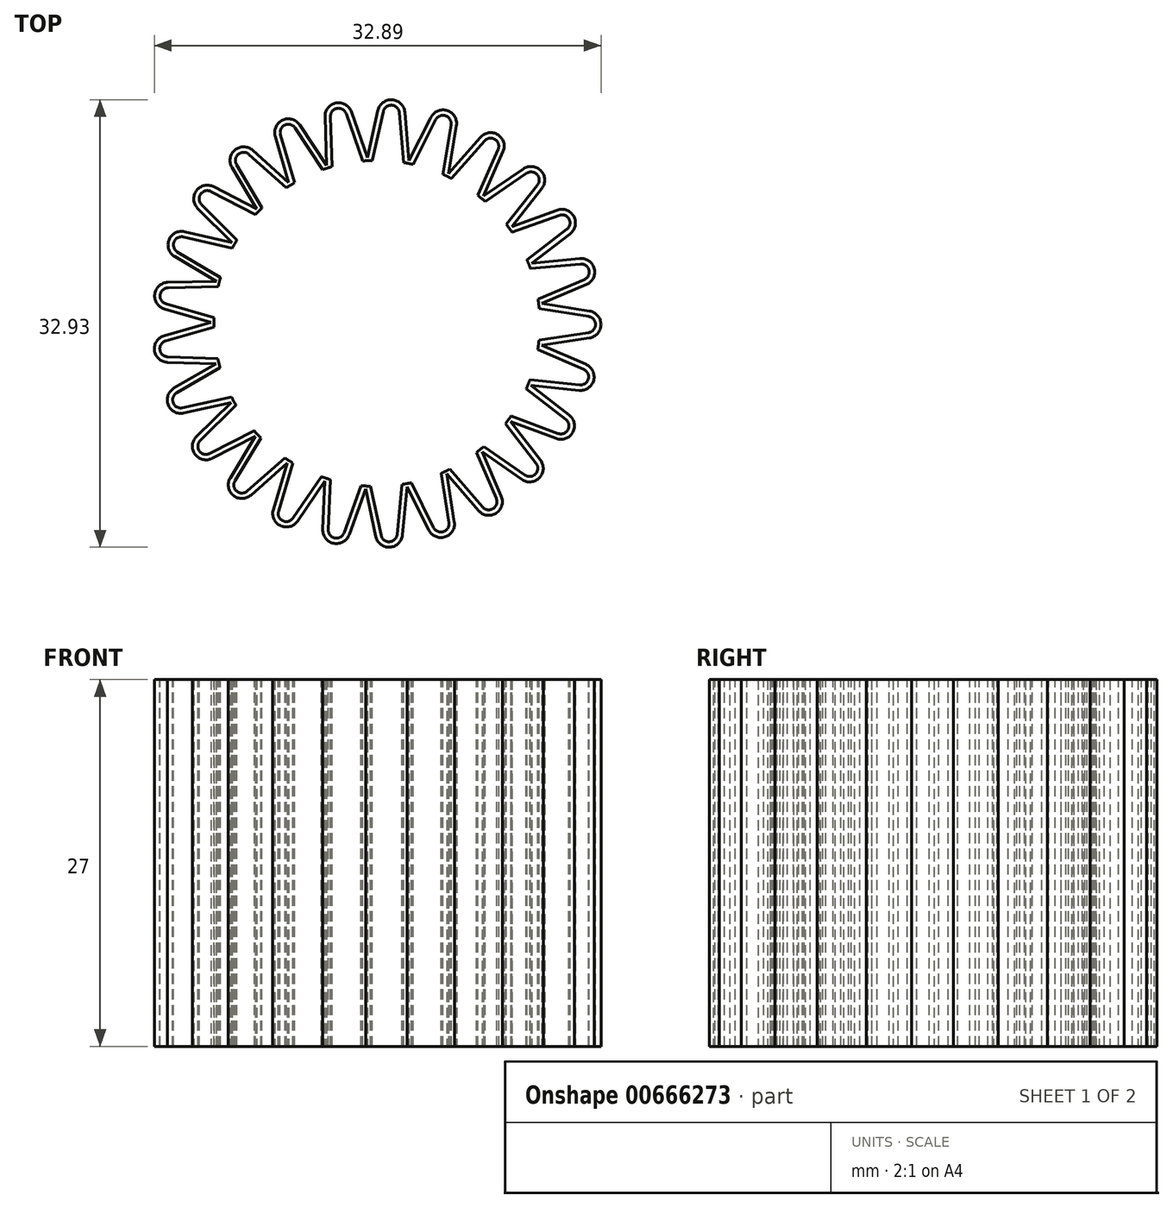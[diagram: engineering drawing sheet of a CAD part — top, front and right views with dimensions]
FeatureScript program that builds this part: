
annotation { "Feature Type Name" : "Feature", "Feature Type Description" : "" }
export const myFeature = defineFeature(function(context is Context, id is Id, definition is map)
    precondition{}
    {
        {
            var Q0;
            Q0=qCreatedBy(makeId("Top.planeOp"),FACE);
            cPlane(context, id + "F0", {"entities" : qUnion([Q0]), "cplaneType" : CPlaneType.OFFSET, "offset" : 13 * mm, "width" : 150 * mm, "height" : 150 * mm});
        }
        {
            var Q0;
            Q0=qCreatedBy(makeId("Front.planeOp"),FACE);
            var sketch = newSketch(context, id + "F1", { "sketchPlane" : qUnion([Q0])});
            skLineSegment(sketch, "E0", {"start": v(0, 0) * mm, "end": v(0, 56.8) * mm, "construction": true});
            skLineSegment(sketch, "E1", {"start": v(-4, 0) * mm, "end": v(-4, 12) * mm, "construction": true});
            skLineSegment(sketch, "E2", {"start": v(-4, 12) * mm, "end": v(-16.5, 12) * mm, "construction": true});
            skLineSegment(sketch, "E3", {"start": v(-16.5, 12) * mm, "end": v(-16.5, 39) * mm, "construction": true});
            skLineSegment(sketch, "E4", {"start": v(-16.5, 39) * mm, "end": v(0, 39) * mm, "construction": true});
            skLineSegment(sketch, "E5", {"start": v(0, 39) * mm, "end": v(0, 40) * mm, "construction": true});
            skLineSegment(sketch, "E6", {"start": v(0, 40) * mm, "end": v(-17.5, 40) * mm, "construction": true});
            skLineSegment(sketch, "E7", {"start": v(-17.5, 40) * mm, "end": v(-17.5, 11) * mm, "construction": true});
            skLineSegment(sketch, "E8", {"start": v(-17.5, 11) * mm, "end": v(-7, 11) * mm, "construction": true});
            skLineSegment(sketch, "E9", {"start": v(-7, 11) * mm, "end": v(-7, 0) * mm, "construction": true});
            skLineSegment(sketch, "E10", {"start": v(-7, 0) * mm, "end": v(-4, 0) * mm, "construction": true});
            skSolve(sketch);
        }
        {
            var Q0;
            Q0=qCreatedBy(id+"F0.planeOp",FACE);
            var sketch = newSketch(context, id + "F2", { "sketchPlane" : qUnion([Q0])});
            skCircle(sketch, "E11", {"center": v(0, 0) * mm, "radius": 16.5 * mm, "construction": true});
            skLineSegment(sketch, "E12", {"start": v(0, 0) * mm, "end": v(-16.5, 0) * mm, "construction": true});
            skLineSegment(sketch, "E13", {"start": v(0, 0) * mm, "end": v(-15.94, 4.27) * mm, "construction": true});
            skCircle(sketch, "E14", {"center": v(0, 0) * mm, "radius": 12 * mm, "construction": true});
            skLineSegment(sketch, "E15", {"start": v(-12, 0) * mm, "end": v(-15.65, 1.06) * mm});
            skLineSegment(sketch, "E16", {"start": v(-15.39, 3.02) * mm, "end": v(-11.6, 3.1) * mm});
            skArc(sketch, "E17", {"start": v(-15.39, 3.02) * mm, "mid": v(-16.36, 2.15) * mm, "end": v(-15.65, 1.06) * mm});
            skArc(sketch, "E18", {"start": v(-11.6, 3.1) * mm, "mid": v(-11.9, 1.57) * mm, "end": v(-12, 0) * mm});
            skSolve(sketch);
        }
        {
            var Q0;
            Q0 = qSketchRegion(id + "F2", true);
            extrude(context, id + "F3", {"entities" : qUnion([Q0]), "depth" : 27 * mm, "offsetDistance" : 25 * mm});
        }
        {
            var Q0;
            Q0=makeQuery(id+"F3.opExtrude","CAP_FACE",FACE,{"disambiguationData":[OSD([sQuery(id+"F2.wireOp",EDGE,"E15"),sQuery(id+"F2.wireOp",EDGE,"E16"),sQuery(id+"F2.wireOp",EDGE,"E17"),sQuery(id+"F2.wireOp",EDGE,"E18")])],"isStart":false});
            var sketch = newSketch(context, id + "F4", { "sketchPlane" : qUnion([Q0])});
            skArc(sketch, "E19", {"start": v(-15.38, 2.62) * mm, "mid": v(-15.96, 2.1) * mm, "end": v(-15.54, 1.45) * mm});
            skLineSegment(sketch, "E20", {"start": v(-15.38, 2.62) * mm, "end": v(-11.7, 2.7) * mm});
            skLineSegment(sketch, "E21", {"start": v(-11.7, 2.7) * mm, "end": v(-12, 0.41) * mm});
            skLineSegment(sketch, "E22", {"start": v(-12, 0.41) * mm, "end": v(-15.54, 1.45) * mm});
            skSolve(sketch);
        }
        {
            var Q0;
            Q0 = qSketchRegion(id + "F4", true);
            extrude(context, id + "F5", {"entities" : qUnion([Q0]), "operationType" : NewBodyOperationType.REMOVE, "endBound" : BoundingType.THROUGH_ALL, "oppositeDirection" : true, "depth" : 25 * mm, "offsetDistance" : 25 * mm});
        }
        {
            var Q0;
            Q0=makeQuery(id+"F3.opExtrude","SWEPT_BODY",BODY,{"disambiguationData":[OSD([sQuery(id+"F2.wireOp",EDGE,"E15"),sQuery(id+"F2.wireOp",EDGE,"E16"),sQuery(id+"F2.wireOp",EDGE,"RT1sCyS9-EH0g-csvh-uenh-4F25LOwI8BUR"),sQuery(id+"F2.wireOp",EDGE,"E17")])]});
            var Q1;
            Q1=sQuery(id+"F2.wireOp",EDGE,"E14");
            circularPattern(context, id + "F6", {"operationType" : NewBodyOperationType.ADD, "entities" : qUnion([Q0]), "axis" : qUnion([Q1]), "angle" : 360 * degree, "instanceCount" : 25, "equalSpace" : true});
        }
    });
